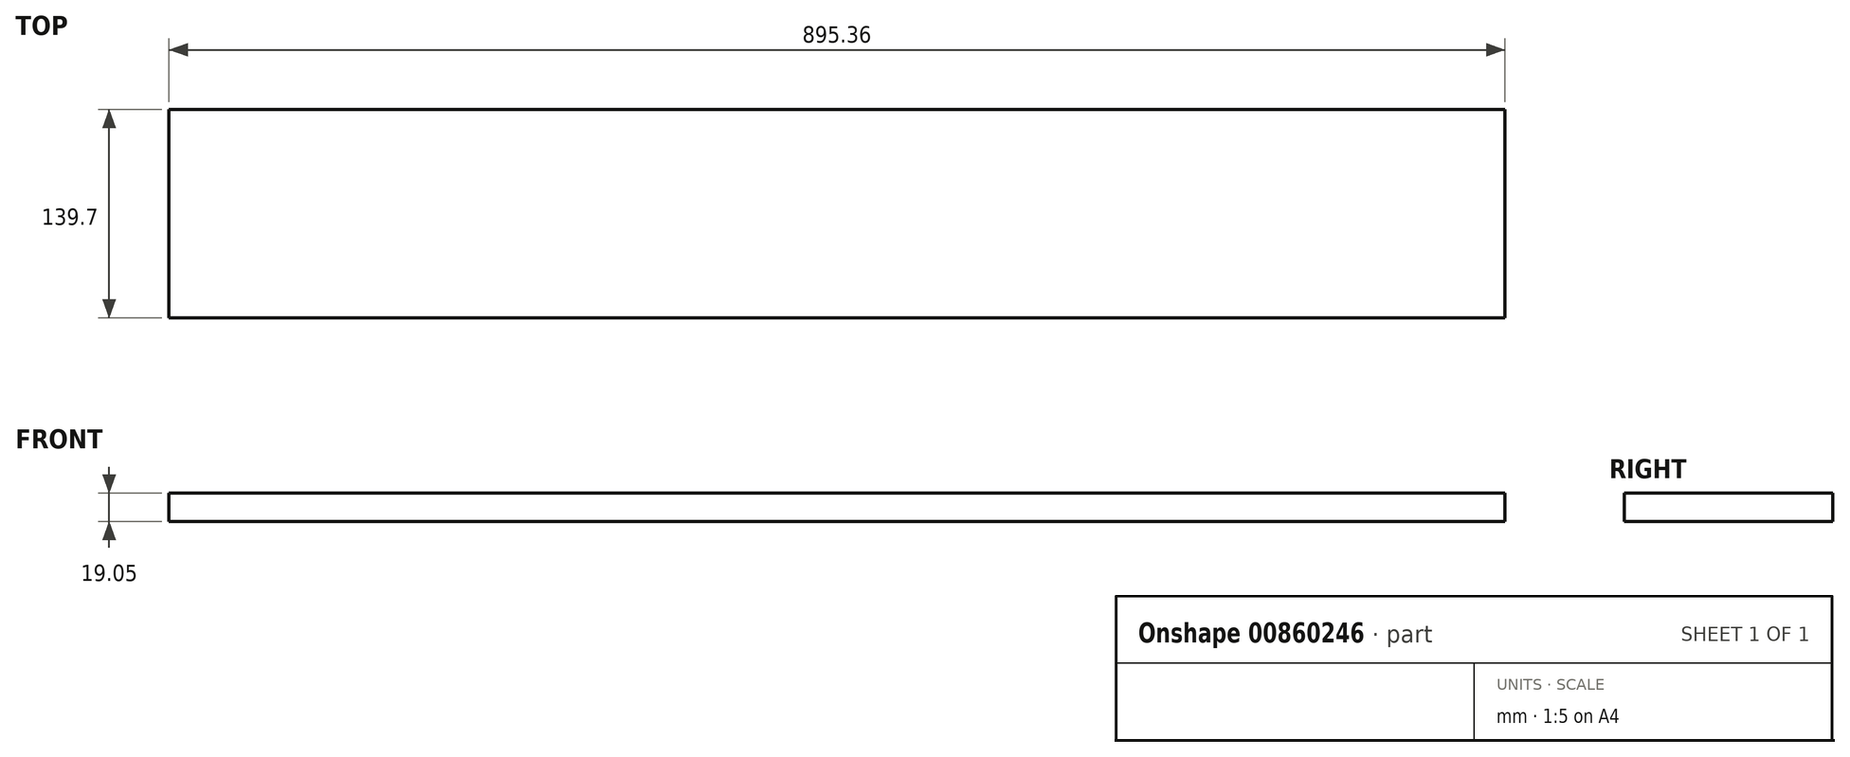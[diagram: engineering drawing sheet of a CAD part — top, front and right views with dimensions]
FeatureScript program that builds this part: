
annotation { "Feature Type Name" : "Feature", "Feature Type Description" : "" }
export const myFeature = defineFeature(function(context is Context, id is Id, definition is map)
    precondition{}
    {
        {
            var Q0;
            Q0=qCreatedBy(makeId("Top.planeOp"),FACE);
            var sketch = newSketch(context, id + "F0", { "sketchPlane" : qUnion([Q0])});
            skLineSegment(sketch, "E0.bottom", {"start": v(447.68, -69.85) * mm, "end": v(-447.68, -69.85) * mm});
            skLineSegment(sketch, "E0.top", {"start": v(447.68, 69.85) * mm, "end": v(-447.68, 69.85) * mm});
            skLineSegment(sketch, "E0.left", {"start": v(447.68, -69.85) * mm, "end": v(447.68, 69.85) * mm});
            skLineSegment(sketch, "E0.right", {"start": v(-447.68, -69.85) * mm, "end": v(-447.68, 69.85) * mm});
            skPoint(sketch, "E0.middle", {"position": v(0, 0) * mm});
            skSolve(sketch);
        }
        {
            var Q0;
            Q0 = qSketchRegion(id + "F0", true);
            extrude(context, id + "F1", {"entities" : qUnion([Q0]), "depth" : 19.05 * mm, "offsetDistance" : 25.4 * mm});
        }
    });
